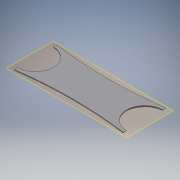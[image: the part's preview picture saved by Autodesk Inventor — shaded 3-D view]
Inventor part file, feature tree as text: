
AUTODESK INVENTOR PART (.ipt)
format: ipt  version: 2017 (Build 210142000, 142)  size: 173,568 bytes
history: native  units: mm
features: reference x5, extrude x3, sketch x3, other x3, plane x1, fillet x1
ambient origin geometry x8: Origin, YZ Plane, XZ Plane, XY Plane, X Axis, Y Axis, Z Axis, Center Point
bodies: Solid1 (feature_tree)
feature tree (16):
  plane  "Work Plane1"
  extrude  "Extrusion1"  Depth=1.0mm
  fillet  "Fillet1"  Radius=0.1mm
  extrude  "Extrusion2"  Depth=2.0mm TaperAngle=0.0deg
  extrude  "Extrusion3"  Depth=1.0mm
  sketch  "Sketch1"  dims[d0=1.0mm d1=0.0mm d2=1.0mm d3=0.1mm]
  reference  "Reference1"
  sketch  "Sketch2"  dims[d4=1.0mm d5=2.0mm d6=0.0mm]
  reference  "Reference2"
  reference  "Reference3"
  reference  "Reference4"
  reference  "Reference5"
  sketch  "Sketch3"  dims[d7=0.25mm d8=0.25mm d9=1.0mm d10=0.0mm d11=1.0mm]
  parser-record x1  (decoder bookkeeping rows leaked as tree rows — omitted from the tree; the rows remain in map.json)
  other  "assembly_full.iam"
  other  "base:1"
note: 1 file-system path scrubbed to <path> (originals preserved in map.json)
